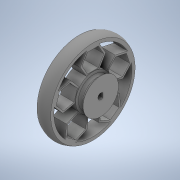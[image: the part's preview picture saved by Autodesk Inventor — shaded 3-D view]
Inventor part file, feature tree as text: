
AUTODESK INVENTOR PART (.ipt)
format: ipt  version: 2020 (Build 240168000, 168)  size: 433,664 bytes
history: native  units: in
note: dims shown in document units (in); Inventor stores cm internally (conversion verified against a paired STEP export)
features: sketch x4, extrude x2, revolve x2, projected_geometry x1
ambient origin geometry x8: Origin, YZ Plane, XZ Plane, XY Plane, X Axis, Y Axis, Z Axis, Center Point
bodies: Solid1 (feature_tree)
feature tree (9):
  extrude  "Extrusion1"  Depth=0.0394in
  sketch  "Sketch3"  dims[d6=0.7087in d7=0.1575in]
  revolve  "Revolution1"  [1 undecoded]
  extrude  "Extrusion2"  Depth=0.1575in
  revolve  "Revolution2"  [1 undecoded]
  sketch  "Sketch1"  dims[d0=0.1181in d1=0.0394in]
  sketch  "Sketch2"  dims[d3=1.6929in d4=0.1181in]
  projected_geometry  "Projected Loop1"
  sketch  "Sketch4"  dims[d8=0.0in d9=1.6929in d10=0.063in d11=0.0315in d16=0.2756in d17=0.0in d19=360.0deg d20=0.0787in d24=0.0394in d25=90.0deg d26=45.0deg d28=0.0079in d29=1.9685in d31=360.0deg]
note: 2 required parameter values undecoded (feature->parameter linkage not recoverable at this tier; creation-order binding heuristic only, values carry confidence <= 0.55)
